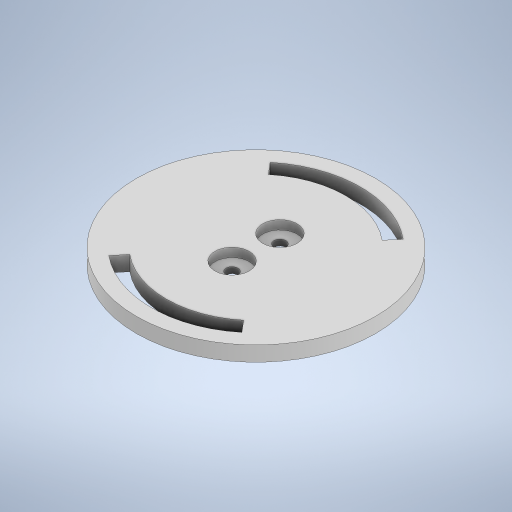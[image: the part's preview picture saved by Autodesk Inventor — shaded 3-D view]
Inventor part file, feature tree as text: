
AUTODESK INVENTOR PART (.ipt)
format: ipt  version: 2023 (Build 270158000, 158)  size: 292,864 bytes
history: native  units: in
note: dims shown in document units (in); Inventor stores cm internally (conversion verified against a paired STEP export)
features: extrude x5, sketch x4, plane x1, mirror x1
ambient origin geometry x8: Origin, YZ Plane, XZ Plane, XY Plane, X Axis, Y Axis, Z Axis, Center Point
bodies: Solid1 (feature_tree)
feature tree (11):
  extrude  "Extrusion1"  Depth=0.1969in TaperAngle=0.0deg
  extrude  "Extrusion3"  Depth=0.9843in
  extrude  "Extrusion5"  Depth=0.9843in
  extrude  "Extrusion7"  Depth=0.1575in TaperAngle=0.0deg
  plane  "Work Plane1"
  mirror  "Mirror1"
  extrude  "Extrusion10"  Depth=0.1969in
  sketch  "Sketch1"  dims[d0=3.1496in d1=0.1969in d2=0.0in]
  sketch  "Sketch6"  dims[d13=0.1969in d14=0.0in d18=0.9843in]
  sketch  "Sketch8"  dims[d19=0.9843in d20=0.7874in]
  sketch  "Sketch11"  dims[d21=0.7874in d22=0.1575in d23=0.0in d46=0.1969in d47=0.1969in d48=0.1181in d49=0.8933in d50=0.1575in d51=0.0in d63=0.315in d64=0.315in d65=0.1575in d66=0.1575in d67=0.4528in d68=0.4528in d69=0.1181in d70=0.0in d10=0.0197in d11=0.0344in d12=0.0197in]
